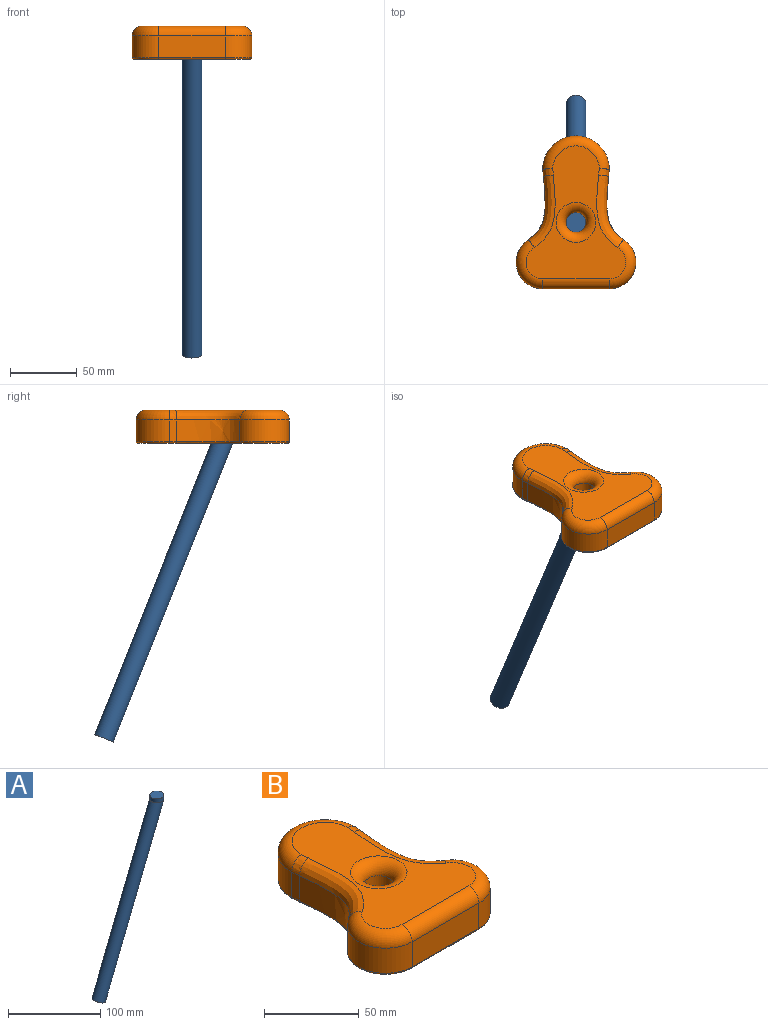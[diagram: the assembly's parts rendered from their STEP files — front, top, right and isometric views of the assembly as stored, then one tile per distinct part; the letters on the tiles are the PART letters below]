
ASSEMBLY  parts=2 mates=1
PART A: 6 faces, bbox 104.2x15x231.3 mm
  f0: plane 15x8.08mm, normal (0,0,1), area 6.8mm2, adj f1,f4
  f1: cylinder r=7.5mm len=231.29mm, axis (0.37,0,0.93), area 11314.3mm2, adj f0,f2,f3
  f2: plane 15x13.93mm, normal (-0.37,0,-0.93), area 176.7mm2, adj f1
  f3: plane 15x8.08mm, normal (0,0,1), area 6.8mm2, adj f1,f4
  f4: cylinder r=7.5mm len=15mm, axis (0,0,-1), area 235.6mm2, adj f0,f3,f5
  f5: plane 15x15mm, normal (0,0,1), area 176.7mm2, adj f4
PART B: 51 faces, bbox 93.3x118.7x25 mm
  f0: extruded ~16.25x5.25mm, area 85.7mm2, adj f1,f8,f15,f45
  f1: cylinder r=25mm len=50mm, axis (0,0,-1), area 1276.3mm2, adj f0,f2,f13,f42
  f2: extruded ~16.25x5.25mm, area 85.7mm2, adj f1,f3,f11,f39
  f3: extruded ~47.75x16.25mm, area 844.4mm2, adj f2,f4,f12,f38
  f4: cylinder r=20mm len=37mm, axis (0,0,-1), area 840.8mm2, adj f3,f5,f14,f41
  f5: plane 50x16.25mm, normal (0,-1,0), area 812.5mm2, adj f4,f6,f16,f44
  f6: cylinder r=20mm len=37.03mm, axis (0,0,-1), area 841.6mm2, adj f5,f8,f18,f46
  f7: cylinder r=7.5mm len=16.25mm, axis (0,0,-1), area 765.8mm2, adj f10,f50
  f8: extruded ~47.73x16.25mm, area 843.7mm2, adj f0,f6,f17,f47
  f9: plane 100x75mm, normal (0,0,1), area 3578mm2, adj f10,f11,f12,f13,f14,f15,f16,f17
  f10: torus R=15mm, axis (0,0,1), area 756.9mm2, adj f7,f9
  f11: bspline ~8.23x8.04mm, area 59.7mm2, adj f2,f9,f12,f13
  f12: bspline ~59.45x21.69mm, area 647.1mm2, adj f3,f9,f11,f14
  f13: torus R=17.5mm, axis (0,0,1), area 819.2mm2, adj f1,f9,f11,f15
  f14: torus R=12.5mm, axis (0,0,1), area 530mm2, adj f4,f9,f12,f16
  f15: bspline ~8.23x8.04mm, area 59.7mm2, adj f0,f9,f13,f17
  f16: cylinder r=7.5mm len=50mm, axis (-1,0,0), area 589mm2, adj f5,f9,f14,f18
  f17: bspline ~70.37x21.47mm, area 646.7mm2, adj f8,f9,f15,f18
  f18: torus R=12.5mm, axis (0,0,1), area 530.5mm2, adj f6,f9,f16,f17
  f19: extruded ~16.25x5.12mm, area 83.6mm2, adj f20,f27,f34,f48
  f20: cylinder r=22.5mm len=45mm, axis (0,0,-1), area 1144.4mm2, adj f19,f21,f32,f42
  f21: extruded ~16.25x5.12mm, area 83.6mm2, adj f20,f22,f30,f43
  f22: extruded ~50.05x16.25mm, area 887mm2, adj f21,f23,f31,f40
  f23: cylinder r=17.5mm len=32.47mm, axis (0,0,-1), area 738.5mm2, adj f22,f24,f33,f41
  f24: plane 50x16.25mm, normal (0,1,0), area 812.5mm2, adj f23,f25,f35,f44
  f25: cylinder r=17.5mm len=32.49mm, axis (0,0,-1), area 739.1mm2, adj f24,f27,f37,f46
  f26: cylinder r=10mm len=20mm, axis (0,0,-1), area 1021mm2, adj f29,f50
  f27: extruded ~50.02x16.25mm, area 886.4mm2, adj f19,f25,f36,f49
  f28: plane 100x75mm, normal (0,0,-1), area 3578mm2, adj f29,f30,f31,f32,f33,f34,f35,f36
  f29: torus R=15mm, axis (0,0,1), area 583.1mm2, adj f26,f28
  f30: bspline ~7.78x5.74mm, area 39.3mm2, adj f21,f28,f31,f32
  f31: bspline ~70.53x20.09mm, area 444.3mm2, adj f22,f28,f30,f33
  f32: torus R=17.5mm, axis (0,0,1), area 506.1mm2, adj f20,f28,f30,f34
  f33: torus R=12.5mm, axis (0,0,1), area 321.5mm2, adj f23,f28,f31,f35
  f34: bspline ~7.78x5.74mm, area 39.3mm2, adj f19,f28,f32,f36
  f35: cylinder r=5mm len=50mm, axis (-1,0,0), area 392.7mm2, adj f24,f28,f33,f37
  f36: bspline ~70.37x19.86mm, area 444.1mm2, adj f27,f28,f34,f37
  f37: torus R=12.5mm, axis (0,0,1), area 321.7mm2, adj f25,f28,f35,f36
  f38: bspline ~65.33x18.83mm, area 103mm2, adj f3,f39,f40,f41
  f39: bspline ~7.36x2.01mm, area 10.3mm2, adj f2,f38,f42,f43
  f40: bspline ~63.67x15.83mm, area 106.2mm2, adj f22,f38,f41,f43
  f41: torus R=18.75mm, axis (0,0,1), area 190.8mm2, adj f4,f23,f38,f40,f44
  f42: torus R=23.75mm, axis (0,0,1), area 292.5mm2, adj f1,f20,f39,f43,f45,f48
  f43: bspline ~7.37x2.01mm, area 10.2mm2, adj f21,f39,f40,f42
  f44: cylinder r=1.25mm len=50mm, axis (1,0,0), area 196.3mm2, adj f5,f24,f41,f46
  f45: bspline ~7.36x2.01mm, area 10.3mm2, adj f0,f42,f47,f48
  f46: torus R=18.75mm, axis (0,0,1), area 191mm2, adj f6,f25,f44,f47,f49
  f47: bspline ~65.2x18.67mm, area 102.9mm2, adj f8,f45,f46,f49
  f48: bspline ~6.54x1.92mm, area 10.2mm2, adj f19,f42,f45,f49
  f49: bspline ~67.16x20.03mm, area 106.2mm2, adj f27,f46,f47,f48
  f50: torus R=8.75mm, axis (0,0,1), area 215.9mm2, adj f7,f26
PLACE A rot(axis=(0,0,-1),90deg) t=(-2.42,88.18,0)mm
PLACE B rot(axis=(0,0,1),0deg) t=(-2.42,45.44,105.62)mm
MATE fastened B.f7 <-> A.f4  axis (0,0,1) through (-2.42,45.44,106.87)mm
